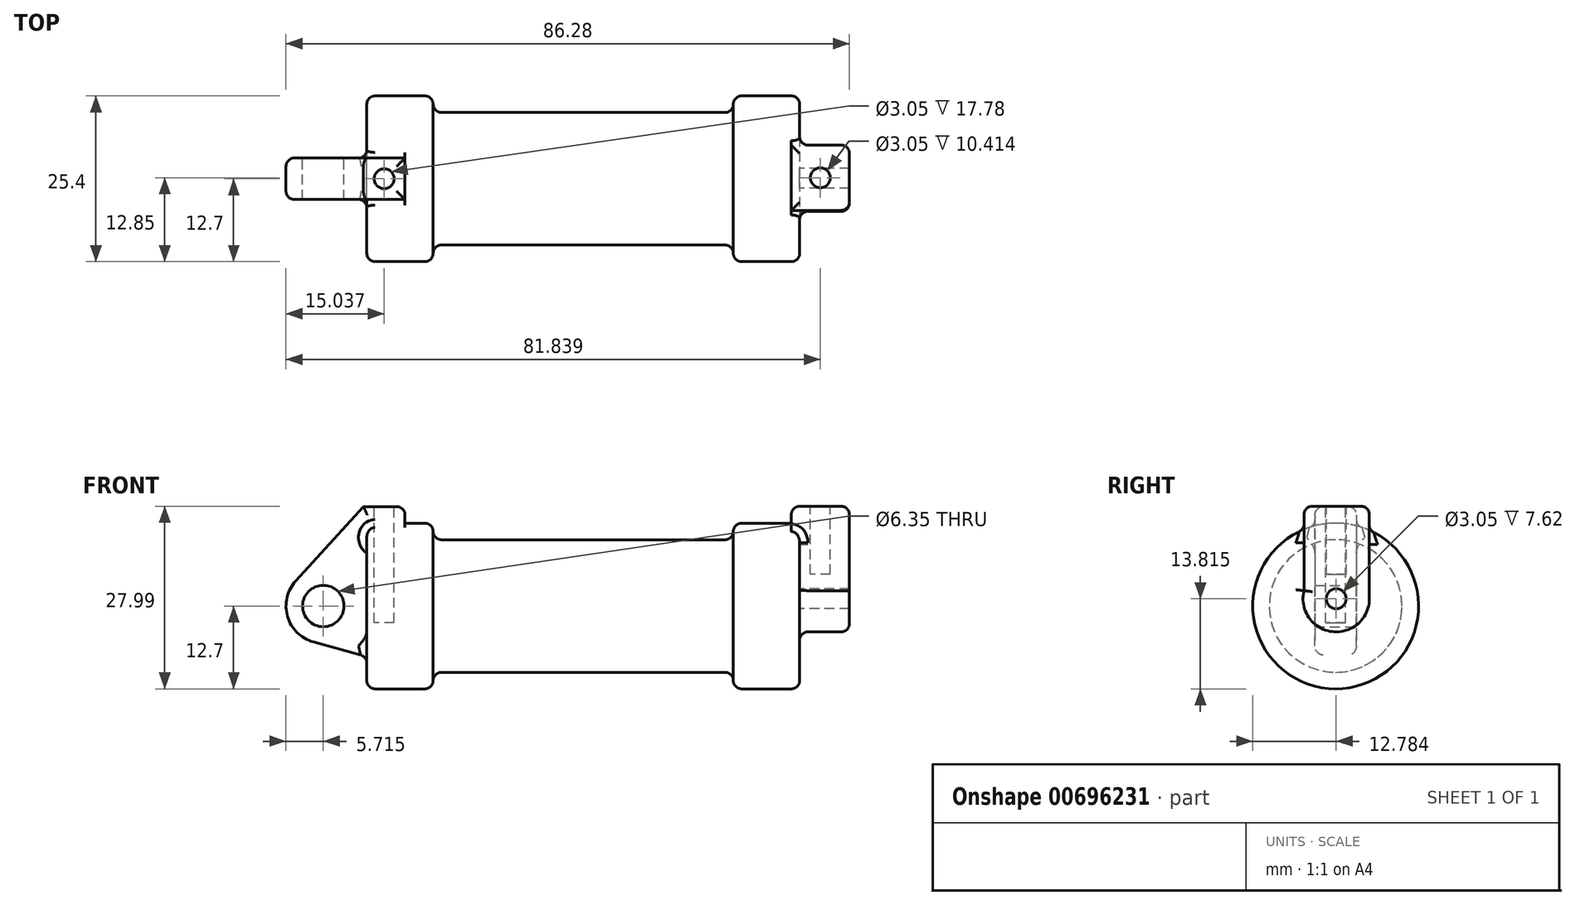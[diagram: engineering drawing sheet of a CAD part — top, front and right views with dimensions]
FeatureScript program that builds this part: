
annotation { "Feature Type Name" : "Feature", "Feature Type Description" : "" }
export const myFeature = defineFeature(function(context is Context, id is Id, definition is map)
    precondition{}
    {
        {
            var Q0;
            Q0=qCreatedBy(makeId("Front.planeOp"),FACE);
            var sketch = newSketch(context, id + "F0", { "sketchPlane" : qUnion([Q0])});
            skLineSegment(sketch, "E0", {"start": v(0, 0) * mm, "end": v(0, 12.7) * mm});
            skLineSegment(sketch, "E1", {"start": v(0, 12.7) * mm, "end": v(10.16, 12.7) * mm});
            skLineSegment(sketch, "E2", {"start": v(10.16, 12.7) * mm, "end": v(10.16, 10.16) * mm});
            skLineSegment(sketch, "E3", {"start": v(10.16, 10.16) * mm, "end": v(56.13, 10.16) * mm});
            skLineSegment(sketch, "E4", {"start": v(56.13, 10.16) * mm, "end": v(56.13, 12.7) * mm});
            skLineSegment(sketch, "E5", {"start": v(56.13, 12.7) * mm, "end": v(66.3, 12.7) * mm});
            skLineSegment(sketch, "E6", {"start": v(66.3, 12.7) * mm, "end": v(66.3, 0) * mm});
            skLineSegment(sketch, "E7", {"start": v(66.3, 0) * mm, "end": v(0, 0) * mm});
            skLineSegment(sketch, "E8", {"start": v(5.84, 15.24) * mm, "end": v(-0.5, 15.24) * mm});
            skLineSegment(sketch, "E9", {"start": v(-0.5, 15.24) * mm, "end": v(-10.88, 3.85) * mm});
            skLineSegment(sketch, "E10", {"start": v(0, 0) * mm, "end": v(-6.65, 0) * mm});
            skCircle(sketch, "E11", {"center": v(-6.65, 0) * mm, "radius": 5.72 * mm});
            skCircle(sketch, "E12", {"center": v(-6.65, 0) * mm, "radius": 3.18 * mm});
            skLineSegment(sketch, "E13", {"start": v(5.84, 15.24) * mm, "end": v(5.84, -9.4) * mm});
            skLineSegment(sketch, "E14", {"start": v(5.84, -9.4) * mm, "end": v(-8.18, -5.5) * mm});
            skSolve(sketch);
        }
        {
            var Q0;
            {var subQ0=sQuery(id+"F0.wireOp",EDGE,"E2");Q0=makeQuery(id+"F0.imprint","IMPRINT",FACE,{"disambiguationData":[TD([[makeQuery(id+"F0.imprint","IMPRINT",EDGE,{"derivedFrom":subQ0}),-1.0]])]});}
            var Q1;
            {var subQ0=sQuery(id+"F0.wireOp",EDGE,"E0");Q1=makeQuery(id+"F0.imprint","IMPRINT",FACE,{"disambiguationData":[TD([[makeQuery(id+"F0.imprint","IMPRINT",EDGE,{"derivedFrom":subQ0}),-1.0]])]});}
            var Q2;
            Q2=sQuery(id+"F0.wireOp",EDGE,"E7");
            revolve(context, id + "F1", {"entities" : qUnion([Q0, Q1]), "axis" : qUnion([Q2]), "revolveType" : RevolveType.FULL});
        }
        {
            var Q0;
            {var subQ1=sQuery(id+"F0.wireOp",EDGE,"E0");Q0=makeQuery(id+"F0.imprint","IMPRINT",FACE,{"disambiguationData":[TD([[makeQuery(id+"F0.imprint","IMPRINT",EDGE,{"derivedFrom":subQ1}),1.0]])]});}
            var Q1;
            {var subQ5=sQuery(id+"F0.wireOp",EDGE,"E12");Q1=makeQuery(id+"F0.imprint","IMPRINT",FACE,{"disambiguationData":[TD([[makeQuery(id+"F0.imprint","IMPRINT",EDGE,{"derivedFrom":subQ5}),-1.0]])]});}
            var Q2;
            {var subQ0=sQuery(id+"F0.wireOp",EDGE,"E14");Q2=makeQuery(id+"F0.imprint","IMPRINT",FACE,{"disambiguationData":[TD([[makeQuery(id+"F0.imprint","IMPRINT",EDGE,{"derivedFrom":subQ0}),-1.0]])]});}
            var Q3;
            {var subQ0=sQuery(id+"F0.wireOp",EDGE,"E0");Q3=makeQuery(id+"F0.imprint","IMPRINT",FACE,{"disambiguationData":[TD([[makeQuery(id+"F0.imprint","IMPRINT",EDGE,{"derivedFrom":subQ0}),-1.0]])]});}
            extrude(context, id + "F2", {"entities" : qUnion([Q0, Q1, Q2, Q3]), "operationType" : NewBodyOperationType.ADD, "endBound" : BoundingType.SYMMETRIC, "depth" : 6.35 * mm, "offsetDistance" : 25.4 * mm});
        }
        {
            var Q0;
            Q0=makeQuery(id+"F1.opRevolve","SWEPT_FACE",FACE,{"disambiguationData":[OSD([sQuery(id+"F0.wireOp",EDGE,"E6")])]});
            var sketch = newSketch(context, id + "F3", { "sketchPlane" : qUnion([Q0])});
            skCircle(sketch, "E15", {"center": v(0.08, 1.11) * mm, "radius": 1.52 * mm});
            skCircle(sketch, "E16", {"center": v(0.08, 1.11) * mm, "radius": 5.08 * mm});
            skLineSegment(sketch, "E17", {"start": v(-4.84, 15.3) * mm, "end": v(5.14, 15.3) * mm});
            skLineSegment(sketch, "E18", {"start": v(-4.84, 15.3) * mm, "end": v(-4.84, 1.4) * mm});
            skLineSegment(sketch, "E19", {"start": v(5.14, 15.3) * mm, "end": v(5.16, 1.12) * mm});
            skSolve(sketch);
        }
        {
            var Q0;
            Q0=makeQuery(id+"F3.imprint","IMPRINT",FACE,{"disambiguationData":[TD([[makeQuery(id+"F3.imprint","IMPRINT",EDGE,{"derivedFrom":sQuery(id+"F3.wireOp",EDGE,"E15")}),-1.0]])]});
            extrude(context, id + "F4", {"entities" : qUnion([Q0]), "operationType" : NewBodyOperationType.ADD, "depth" : 7.62 * mm, "offsetDistance" : 25.4 * mm});
        }
        {
            var Q0;
            Q0 = qSketchRegion(id + "F3", true);
            extrude(context, id + "F5", {"entities" : qUnion([Q0]), "operationType" : NewBodyOperationType.ADD, "depth" : 7.62 * mm, "offsetDistance" : 25.4 * mm});
        }
        {
            var Q0;
            Q0 = qSketchRegion(id + "F3", true);
            extrude(context, id + "F6", {"entities" : qUnion([Q0]), "operationType" : NewBodyOperationType.ADD, "oppositeDirection" : true, "depth" : 1.27 * mm, "offsetDistance" : 25.4 * mm});
        }
        {
            var Q0;
            Q0=makeQuery(id+"F2.opExtrude","SWEPT_FACE",FACE,{"disambiguationData":[OSD([sQuery(id+"F0.wireOp",EDGE,"E8")])]});
            var sketch = newSketch(context, id + "F7", { "sketchPlane" : qUnion([Q0])});
            skLineSegment(sketch, "E20", {"start": v(2.67, 3.18) * mm, "end": v(2.64, 3.3) * mm});
            skCircle(sketch, "E21", {"center": v(2.67, 0) * mm, "radius": 1.52 * mm});
            skSolve(sketch);
        }
        {
            var Q0;
            {var subQ0=sQuery(id+"F3.wireOp",EDGE,"E17");Q0=makeQuery(id+"F6.boolean.opBoolean","MERGE",FACE,{"derivedFrom":[makeQuery(id+"F5.opExtrude","SWEPT_FACE",FACE,{"disambiguationData":[OSD([subQ0])]}),makeQuery(id+"F6.opExtrude","SWEPT_FACE",FACE,{"disambiguationData":[OSD([subQ0])]})]});}
            var sketch = newSketch(context, id + "F8", { "sketchPlane" : qUnion([Q0])});
            skCircle(sketch, "E22", {"center": v(69.47, 0.15) * mm, "radius": 1.52 * mm});
            skSolve(sketch);
        }
        {
            var Q0;
            Q0=makeQuery(id+"F7.imprint","IMPRINT",FACE,{"disambiguationData":[TD([[makeQuery(id+"F7.imprint","IMPRINT",EDGE,{"derivedFrom":sQuery(id+"F7.wireOp",EDGE,"E21")}),1.0]])]});
            extrude(context, id + "F9", {"entities" : qUnion([Q0]), "operationType" : NewBodyOperationType.REMOVE, "oppositeDirection" : true, "depth" : 17.78 * mm, "offsetDistance" : 25.4 * mm});
        }
        {
            var Q0;
            Q0=makeQuery(id+"F8.imprint","IMPRINT",FACE,{"disambiguationData":[TD([[makeQuery(id+"F8.imprint","IMPRINT",EDGE,{"derivedFrom":sQuery(id+"F8.wireOp",EDGE,"E22")}),1.0]])]});
            extrude(context, id + "F10", {"entities" : qUnion([Q0]), "operationType" : NewBodyOperationType.REMOVE, "oppositeDirection" : true, "depth" : 10.4 * mm, "offsetDistance" : 25.4 * mm});
        }
        {
            var Q0;
            Q0=makeQuery(id+"F1.opRevolve","SWEPT_EDGE",EDGE,{"disambiguationData":[OSD([sQuery(id+"F0.wireOp",EDGE,"E4"),sQuery(id+"F0.wireOp",EDGE,"E5")])]});
            var Q1;
            Q1=makeQuery(id+"F1.opRevolve","SWEPT_FACE",FACE,{"disambiguationData":[OSD([sQuery(id+"F0.wireOp",EDGE,"E3")])]});
            var Q2;
            {var subQ0=sQuery(id+"F0.wireOp",EDGE,"E5");var subQ1=sQuery(id+"F0.wireOp",EDGE,"E6");Q2=makeQuery(id+"F5.boolean.opBoolean","SPLIT",EDGE,{"disambiguationData":[topologyDisambiguationEdgeConnected([makeQuery(id+"F1.opRevolve","SWEPT_FACE",FACE,{"disambiguationData":[OSD([subQ1])]})])],"derivedFrom":makeQuery(id+"F1.opRevolve","SWEPT_EDGE",EDGE,{"disambiguationData":[OSD([subQ0,subQ1])]})});}
            var Q3;
            {var subQ0=sQuery(id+"F3.wireOp",EDGE,"E18");var subQ1=sQuery(id+"F3.wireOp",EDGE,"E17");Q3=makeQuery(id+"F6.boolean.opBoolean","MERGE",EDGE,{"derivedFrom":[makeQuery(id+"F5.opExtrude","SWEPT_EDGE",EDGE,{"disambiguationData":[OSD([subQ1,subQ0])]}),makeQuery(id+"F6.opExtrude","SWEPT_EDGE",EDGE,{"disambiguationData":[OSD([subQ1,subQ0])]})]});}
            var Q4;
            Q4=makeQuery(id+"F6.opExtrude","CAP_EDGE",EDGE,{"disambiguationData":[OSD([sQuery(id+"F3.wireOp",EDGE,"E17")])],"isStart":false});
            var Q5;
            {var subQ0=sQuery(id+"F3.wireOp",EDGE,"E19");var subQ1=sQuery(id+"F3.wireOp",EDGE,"E17");Q5=makeQuery(id+"F6.boolean.opBoolean","MERGE",EDGE,{"derivedFrom":[makeQuery(id+"F5.opExtrude","SWEPT_EDGE",EDGE,{"disambiguationData":[OSD([subQ1,subQ0])]}),makeQuery(id+"F6.opExtrude","SWEPT_EDGE",EDGE,{"disambiguationData":[OSD([subQ1,subQ0])]})]});}
            var Q6;
            Q6=makeQuery(id+"F2.boolean.opBoolean","INTERSECT",EDGE,{"derivedFrom":[makeQuery(id+"F1.opRevolve","SWEPT_FACE",FACE,{"disambiguationData":[OSD([sQuery(id+"F0.wireOp",EDGE,"E1")])]}),makeQuery(id+"F2.opExtrude","CAP_FACE",FACE,{"disambiguationData":[OSD([sQuery(id+"F0.wireOp",EDGE,"E8"),sQuery(id+"F0.wireOp",EDGE,"E9"),sQuery(id+"F0.wireOp",EDGE,"E11"),sQuery(id+"F0.wireOp",EDGE,"E12"),sQuery(id+"F0.wireOp",EDGE,"E13"),sQuery(id+"F0.wireOp",EDGE,"E14")])],"isStart":false})]});
            var Q7;
            Q7=makeQuery(id+"F1.opRevolve","SWEPT_EDGE",EDGE,{"disambiguationData":[OSD([sQuery(id+"F0.wireOp",EDGE,"E0"),sQuery(id+"F0.wireOp",EDGE,"E1")])]});
            var Q8;
            Q8=makeQuery(id+"F1.opRevolve","SWEPT_EDGE",EDGE,{"disambiguationData":[OSD([sQuery(id+"F0.wireOp",EDGE,"E1"),sQuery(id+"F0.wireOp",EDGE,"E2")])]});
            var Q9;
            Q9=makeQuery(id+"F2.opExtrude","CAP_EDGE",EDGE,{"disambiguationData":[OSD([sQuery(id+"F0.wireOp",EDGE,"E8")])],"isStart":true});
            var Q10;
            Q10=makeQuery(id+"F2.boolean.opBoolean","INTERSECT",EDGE,{"derivedFrom":[makeQuery(id+"F1.opRevolve","SWEPT_FACE",FACE,{"disambiguationData":[OSD([sQuery(id+"F0.wireOp",EDGE,"E1")])]}),makeQuery(id+"F2.opExtrude","CAP_FACE",FACE,{"disambiguationData":[OSD([sQuery(id+"F0.wireOp",EDGE,"E8"),sQuery(id+"F0.wireOp",EDGE,"E9"),sQuery(id+"F0.wireOp",EDGE,"E11"),sQuery(id+"F0.wireOp",EDGE,"E12"),sQuery(id+"F0.wireOp",EDGE,"E13"),sQuery(id+"F0.wireOp",EDGE,"E14")])],"isStart":true})]});
            var Q11;
            Q11=makeQuery(id+"F2.boolean.opBoolean","INTERSECT",EDGE,{"derivedFrom":[makeQuery(id+"F1.opRevolve","SWEPT_FACE",FACE,{"disambiguationData":[OSD([sQuery(id+"F0.wireOp",EDGE,"E0")])]}),makeQuery(id+"F2.opExtrude","SWEPT_FACE",FACE,{"disambiguationData":[OSD([sQuery(id+"F0.wireOp",EDGE,"E14")])]})]});
            var Q12;
            Q12=makeQuery(id+"F4.opExtrude","CAP_EDGE",EDGE,{"disambiguationData":[OSD([sQuery(id+"F3.wireOp",EDGE,"E16")])],"isStart":true});
            var Q13;
            {var subQ0=sQuery(id+"F3.wireOp",EDGE,"E19");Q13=makeQuery(id+"F5.boolean.opBoolean","SPLIT",EDGE,{"disambiguationData":[topologyDisambiguationEdgeConnected([makeQuery(id+"F1.opRevolve","SWEPT_FACE",FACE,{"disambiguationData":[OSD([sQuery(id+"F0.wireOp",EDGE,"E6")])]})])],"derivedFrom":makeQuery(id+"F5.opExtrude","CAP_EDGE",EDGE,{"disambiguationData":[OSD([subQ0])],"isStart":true})});}
            var Q14;
            Q14=makeQuery(id+"F4.boolean.opBoolean","SPLIT",FACE,{"disambiguationData":[TD([makeQuery(id+"F1.opRevolve","SWEPT_FACE",FACE,{"disambiguationData":[OSD([sQuery(id+"F0.wireOp",EDGE,"E5")])]})])],"derivedFrom":makeQuery(id+"F1.opRevolve","SWEPT_FACE",FACE,{"disambiguationData":[OSD([sQuery(id+"F0.wireOp",EDGE,"E6")])]})});
            var Q15;
            Q15=makeQuery(id+"F5.opExtrude","CAP_EDGE",EDGE,{"disambiguationData":[OSD([sQuery(id+"F3.wireOp",EDGE,"E17")])],"isStart":false});
            var Q16;
            Q16=makeQuery(id+"F5.opExtrude","CAP_EDGE",EDGE,{"disambiguationData":[OSD([sQuery(id+"F3.wireOp",EDGE,"E18")])],"isStart":false});
            var Q17;
            Q17=makeQuery(id+"F4.opExtrude","CAP_EDGE",EDGE,{"disambiguationData":[OSD([sQuery(id+"F3.wireOp",EDGE,"E16")])],"isStart":false});
            var Q18;
            Q18=makeQuery(id+"F2.opExtrude","CAP_EDGE",EDGE,{"disambiguationData":[OSD([sQuery(id+"F0.wireOp",EDGE,"E9")])],"isStart":true});
            var Q19;
            Q19=makeQuery(id+"F2.opExtrude","CAP_EDGE",EDGE,{"disambiguationData":[OSD([sQuery(id+"F0.wireOp",EDGE,"E11")])],"isStart":false});
            var Q20;
            Q20=makeQuery(id+"F2.opExtrude","SWEPT_EDGE",EDGE,{"disambiguationData":[OSD([sQuery(id+"F0.wireOp",EDGE,"E8"),sQuery(id+"F0.wireOp",EDGE,"E13")])]});
            var Q21;
            Q21=makeQuery(id+"F2.opExtrude","CAP_EDGE",EDGE,{"disambiguationData":[OSD([sQuery(id+"F0.wireOp",EDGE,"E8")])],"isStart":false});
            fillet(context, id + "F11", {"entities" : qUnion([Q0, Q1, Q2, Q3, Q4, Q5, Q6, Q7, Q8, Q9, Q10, Q11, Q12, Q13, Q14, Q15, Q16, Q17, Q18, Q19, Q20, Q21]), "radius" : 1.27 * mm, "tangentPropagation" : true, "allowEdgeOverflow" : false});
        }
    });
